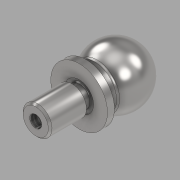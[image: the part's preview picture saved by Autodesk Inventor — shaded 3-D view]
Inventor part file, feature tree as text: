
AUTODESK INVENTOR PART (.ipt)
format: ipt  version: 2020 (Build 240168000, 168)  size: 176,128 bytes
history: native  units: in
note: dims shown in document units (in); Inventor stores cm internally (conversion verified against a paired STEP export)
features: fillet x2, sketch x2, other x1, revolve x1, chamfer x1, hole x1
ambient origin geometry x8: Origin, YZ Plane, XZ Plane, XY Plane, X Axis, Y Axis, Z Axis, Center Point
bodies: Body1 (feature_tree)
feature tree (8):
  other  "Sólido1"
  revolve  "Revolución1"  [1 undecoded]
  fillet  "Empalme_016"  Radius=0.375in
  fillet  "Empalme_031"  Radius=0.5in
  chamfer  "Chaflán1"  Distance=0.375in
  hole  "Agujero1"  [1 undecoded]
  sketch  "Boceto1"  dims[d0=0.25in d1=0.49in d2=0.375in d3=0.5in]
  sketch  "Boceto2"  dims[d4=0.313in d5=0.375in d7=0.688in d8=0.435in d9=0.016in d10=0.032in d11=0.375in d12=90.0deg d13=0.016in d15=0.031in d16=0.016in d17=0.125in d18=45.0deg d19=0.104in d20=0.181in d21=0.5in d22=0.3in d23=0.5635in d24=0.313in d25=0.8108in]
note: 2 required parameter values undecoded (feature->parameter linkage not recoverable at this tier; creation-order binding heuristic only, values carry confidence <= 0.55)